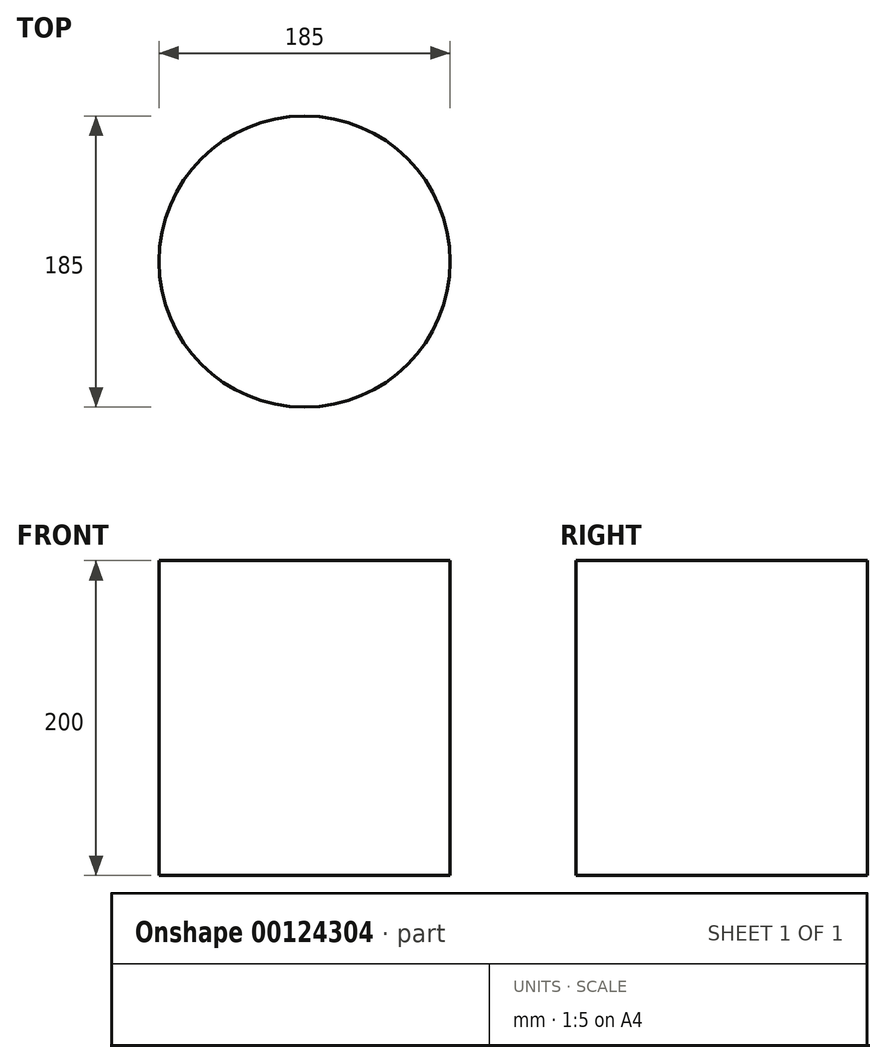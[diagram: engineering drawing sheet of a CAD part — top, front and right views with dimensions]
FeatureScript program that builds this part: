
annotation { "Feature Type Name" : "Feature", "Feature Type Description" : "" }
export const myFeature = defineFeature(function(context is Context, id is Id, definition is map)
    precondition{}
    {
        {
            var Q0;
            Q0=qCreatedBy(makeId("Top.planeOp"),FACE);
            var sketch = newSketch(context, id + "F0", { "sketchPlane" : qUnion([Q0])});
            skCircle(sketch, "E0", {"center": v(0, 0) * mm, "radius": 92.5 * mm});
            skSolve(sketch);
        }
        {
            var Q0;
            Q0 = qSketchRegion(id + "F0", true);
            extrude(context, id + "F1", {"entities" : qUnion([Q0]), "depth" : 200 * mm});
        }
    });
